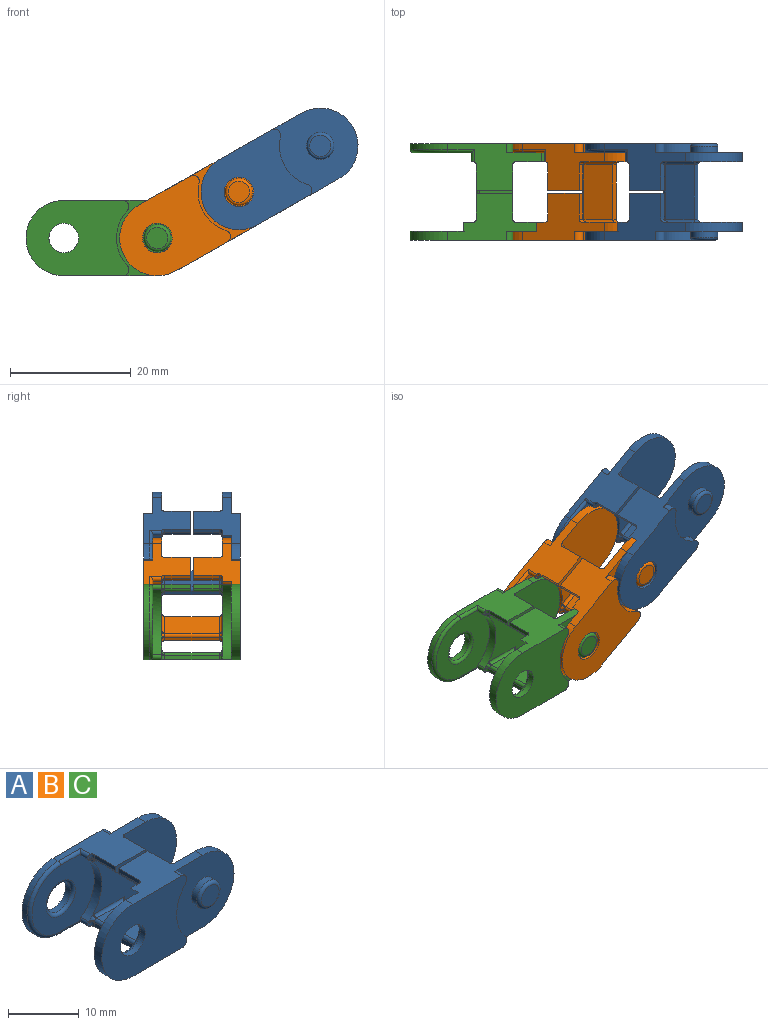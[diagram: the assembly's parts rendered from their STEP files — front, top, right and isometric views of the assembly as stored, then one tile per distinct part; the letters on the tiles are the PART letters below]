
ASSEMBLY  parts=3 mates=4
PART A: 80 faces, bbox 28.5x16x13.5 mm
  f0: plane 5.5x4.25mm, normal (0,0,-1), area 23.4mm2, adj f24,f48,f57,f79
  f1: plane 15.5x7.75mm, normal (0,0,1), area 62.7mm2, adj f2,f3,f7,f9,f10,f16,f19,f28
  f2: plane 4.25x1.2mm, normal (1,0,0), area 5.1mm2, adj f1,f26,f50,f78
  f3: plane 4.25x0.7mm, normal (-1,0,0), area 3mm2, adj f1,f4,f55,f78
  f4: cylinder r=0.5mm len=4.25mm, axis (0,1,0), area 3.3mm2, adj f3,f26,f52,f53,f54,f78
  f5: plane 1.03x0.4mm, normal (0,-1,0), area 0.2mm2, adj f39,f43,f60,f61
  f6: plane 1.03x0.4mm, normal (0,-1,0), area 0.2mm2, adj f39,f46,f66,f67
  f7: plane 1.77x1.06mm, normal (0,1,0), area 0.8mm2, adj f1,f41,f54,f55
  f8: plane 1.77x1.06mm, normal (0,1,0), area 0.8mm2, adj f18,f41,f72,f73
  f9: plane 16.81x12.5mm, normal (0,1,0), area 160.5mm2, adj f1,f16,f18,f41,f50,f51,f52,f68
  f10: cylinder r=6.25mm len=12.5mm, axis (0,1,0), area 29.5mm2, adj f1,f18,f19,f42
  f11: cylinder r=2.45mm len=4.9mm, axis (0,-1,0), area 15.4mm2, adj f19,f74
  f12: cylinder r=6.25mm len=12.5mm, axis (0,1,0), area 19.6mm2, adj f15,f18,f20,f45
  f13: cylinder r=2.45mm len=4.9mm, axis (0,-1,0), area 15.4mm2, adj f15,f75
  f14: cylinder r=6.25mm len=12.5mm, axis (0,-1,0), area 29.5mm2, adj f18,f20,f21,f30
  f15: plane 17.05x12.5mm, normal (0,1,0), area 163.3mm2, adj f12,f13,f18,f20,f29,f31,f32
  f16: cylinder r=6.25mm len=12.5mm, axis (0,-1,0), area 29.5mm2, adj f1,f9,f18,f28
  f17: plane 9x0.7mm, normal (-1,0,0), area 6.3mm2, adj f18,f49,f67,f73
  f18: plane 16x15.5mm, normal (0,0,-1), area 123.5mm2, adj f8,f9,f10,f12,f14,f15,f16,f17
  f19: plane 17.05x12.5mm, normal (0,-1,0), area 163.3mm2, adj f1,f10,f11,f18,f27,f33,f34
  f20: plane 15.5x7.75mm, normal (0,0,1), area 57.7mm2, adj f12,f14,f15,f21,f24,f25,f30,f32
  f21: plane 16.81x12.5mm, normal (0,-1,0), area 160.5mm2, adj f14,f18,f20,f39,f56,f57,f58,f62
  f22: plane 9x1.2mm, normal (1,0,0), area 10.8mm2, adj f18,f23,f62,f68
  f23: plane 9x5.5mm, normal (0,0,1), area 49.5mm2, adj f22,f49,f63,f69
  f24: plane 4.25x1.2mm, normal (1,0,0), area 5.1mm2, adj f0,f20,f56,f79
  f25: plane 4.25x0.7mm, normal (-1,0,0), area 3mm2, adj f20,f48,f61,f79
  f26: plane 5.5x4.25mm, normal (0,0,-1), area 23.4mm2, adj f2,f4,f51,f78
  f27: cylinder r=6.75mm len=9.15mm, axis (0,-1,0), area 15.1mm2, adj f19,f28,f33,f34
  f28: plane 13x12.5mm, normal (0,-1,0), area 118.4mm2, adj f1,f16,f18,f27,f33,f34,f35
  f29: cylinder r=6.75mm len=9.15mm, axis (0,1,0), area 15.1mm2, adj f15,f30,f31,f32
  f30: plane 13x12.5mm, normal (0,1,0), area 118.4mm2, adj f14,f18,f20,f29,f31,f32,f37
  f31: cylinder r=1mm len=1.68mm, axis (0,1,0), area 3.5mm2, adj f15,f18,f29,f30
  f32: cylinder r=1mm len=1.68mm, axis (0,1,0), area 3.5mm2, adj f15,f20,f29,f30
  f33: cylinder r=1mm len=1.68mm, axis (0,-1,0), area 3.5mm2, adj f18,f19,f27,f28
  f34: cylinder r=1mm len=1.68mm, axis (0,-1,0), area 3.5mm2, adj f1,f19,f27,f28
  f35: cylinder r=2.25mm len=4.5mm, axis (0,1,0), area 14.1mm2, adj f28,f77
  f36: plane 3.5x3.5mm, normal (0,-1,0), area 9.6mm2, adj f77
  f37: cylinder r=2.25mm len=4.5mm, axis (0,-1,0), area 14.1mm2, adj f30,f76
  f38: plane 3.5x3.5mm, normal (0,1,0), area 9.6mm2, adj f76
  f39: cylinder r=6.75mm len=10.71mm, axis (0,-1,0), area 18.5mm2, adj f5,f6,f21,f40,f43,f46,f59,f65
  f40: plane 12.5x11.5mm, normal (0,-1,0), area 91.5mm2, adj f39,f43,f44,f45,f46,f47,f75
  f41: cylinder r=6.75mm len=12.5mm, axis (0,1,0), area 24mm2, adj f1,f7,f8,f9,f18,f42,f53,f71
  f42: plane 13x12.5mm, normal (0,1,0), area 103.9mm2, adj f1,f10,f18,f41,f74
  f43: cylinder r=0.5mm len=2.03mm, axis (0,-1,0), area 2mm2, adj f5,f20,f39,f40,f44,f61
  f44: cylinder r=0.5mm len=4.42mm, axis (1,0,0), area 3.2mm2, adj f20,f40,f43,f45
  f45: torus R=5.75mm, axis (0,-1,0), area 15mm2, adj f12,f40,f44,f47
  f46: cylinder r=0.5mm len=2.03mm, axis (0,-1,0), area 2mm2, adj f6,f18,f39,f40,f47,f67
  f47: cylinder r=0.5mm len=4.42mm, axis (-1,0,0), area 3.2mm2, adj f18,f40,f45,f46
  f48: cylinder r=0.5mm len=4.25mm, axis (0,1,0), area 3.3mm2, adj f0,f25,f58,f59,f60,f79
  f49: cylinder r=0.5mm len=9mm, axis (0,-1,0), area 7.1mm2, adj f17,f23,f64,f65,f66,f70,f71,f72
  f50: cylinder r=0.5mm len=1.7mm, axis (0,0,-1), area 1.1mm2, adj f1,f2,f9,f51
  f51: cylinder r=0.5mm len=6mm, axis (-1,0,0), area 4.5mm2, adj f9,f26,f50,f52
  f52: torus R=1mm, axis (0,-1,0), area 0.2mm2, adj f4,f9,f51,f53
  f53: bspline ~0.93x0.92mm, area 0.4mm2, adj f4,f41,f52,f54
  f54: torus R=1mm, axis (0,-1,0), area 0.2mm2, adj f4,f7,f53,f55
  f55: cylinder r=0.5mm len=0.7mm, axis (0,0,1), area 0.5mm2, adj f1,f3,f7,f54
  f56: cylinder r=0.5mm len=1.7mm, axis (0,0,1), area 1.1mm2, adj f20,f21,f24,f57
  f57: cylinder r=0.5mm len=6mm, axis (-1,0,0), area 4.5mm2, adj f0,f21,f56,f58
  f58: torus R=1mm, axis (0,-1,0), area 0.2mm2, adj f21,f48,f57,f59
  f59: bspline ~0.93x0.92mm, area 0.4mm2, adj f39,f48,f58,f60
  f60: torus R=1mm, axis (0,-1,0), area 0.2mm2, adj f5,f48,f59,f61
  f61: cylinder r=0.5mm len=0.7mm, axis (0,0,-1), area 0.5mm2, adj f5,f20,f25,f43,f60
  f62: cylinder r=0.5mm len=1.7mm, axis (0,0,-1), area 1.1mm2, adj f18,f21,f22,f63
  f63: cylinder r=0.5mm len=6mm, axis (-1,0,0), area 4.5mm2, adj f21,f23,f62,f64
  f64: torus R=1mm, axis (0,-1,0), area 0.2mm2, adj f21,f49,f63,f65
  f65: bspline ~0.93x0.92mm, area 0.4mm2, adj f39,f49,f64,f66
  f66: torus R=1mm, axis (0,-1,0), area 0.2mm2, adj f6,f49,f65,f67
  f67: cylinder r=0.5mm len=0.7mm, axis (0,0,1), area 0.5mm2, adj f6,f17,f18,f46,f66
  f68: cylinder r=0.5mm len=1.7mm, axis (0,0,1), area 1.1mm2, adj f9,f18,f22,f69
  f69: cylinder r=0.5mm len=6mm, axis (1,0,0), area 4.5mm2, adj f9,f23,f68,f70
  f70: torus R=1mm, axis (0,-1,0), area 0.2mm2, adj f9,f49,f69,f71
  f71: bspline ~0.93x0.92mm, area 0.4mm2, adj f41,f49,f70,f72
  f72: torus R=1mm, axis (0,-1,0), area 0.2mm2, adj f8,f49,f71,f73
  f73: cylinder r=0.5mm len=0.7mm, axis (0,0,-1), area 0.5mm2, adj f8,f17,f18,f72
  f74: torus R=2.95mm, axis (0,1,0), area 13mm2, adj f11,f42
  f75: torus R=2.95mm, axis (0,-1,0), area 13mm2, adj f13,f40
  f76: torus R=1.75mm, axis (0,1,0), area 10.2mm2, adj f37,f38
  f77: torus R=1.75mm, axis (0,-1,0), area 10.2mm2, adj f35,f36
  f78: plane 6x1.2mm, normal (0,1,0), area 7.1mm2, adj f1,f2,f3,f4,f26
  f79: plane 6x1.2mm, normal (0,-1,0), area 7.1mm2, adj f0,f20,f24,f25,f48
PART B: same geometry as A
PART C: same geometry as A
PLACE A rot(axis=(0,-1,0),29.5deg) t=(27.48,-0.18,11.62)mm
PLACE B rot(axis=(0,-1,0),29.5deg) t=(13.99,-0.18,3.99)mm
PLACE C t=(-0.5,-0.18,0.17)mm fixed
MATE cylindrical A.f10 <-> B.f27  axis (0,-1,0) through (20.73,-8.18,7.81)mm
MATE planar B.f10 <-> C.f28  axis (0,1,0) through (7.25,-6.68,0.17)mm
MATE cylindrical C.f27 <-> B.f10  axis (0,-1,0) through (7.25,-8.18,0.17)mm
MATE planar A.f42 <-> B.f28  axis (0,1,0) through (17.66,-6.68,13.24)mm
